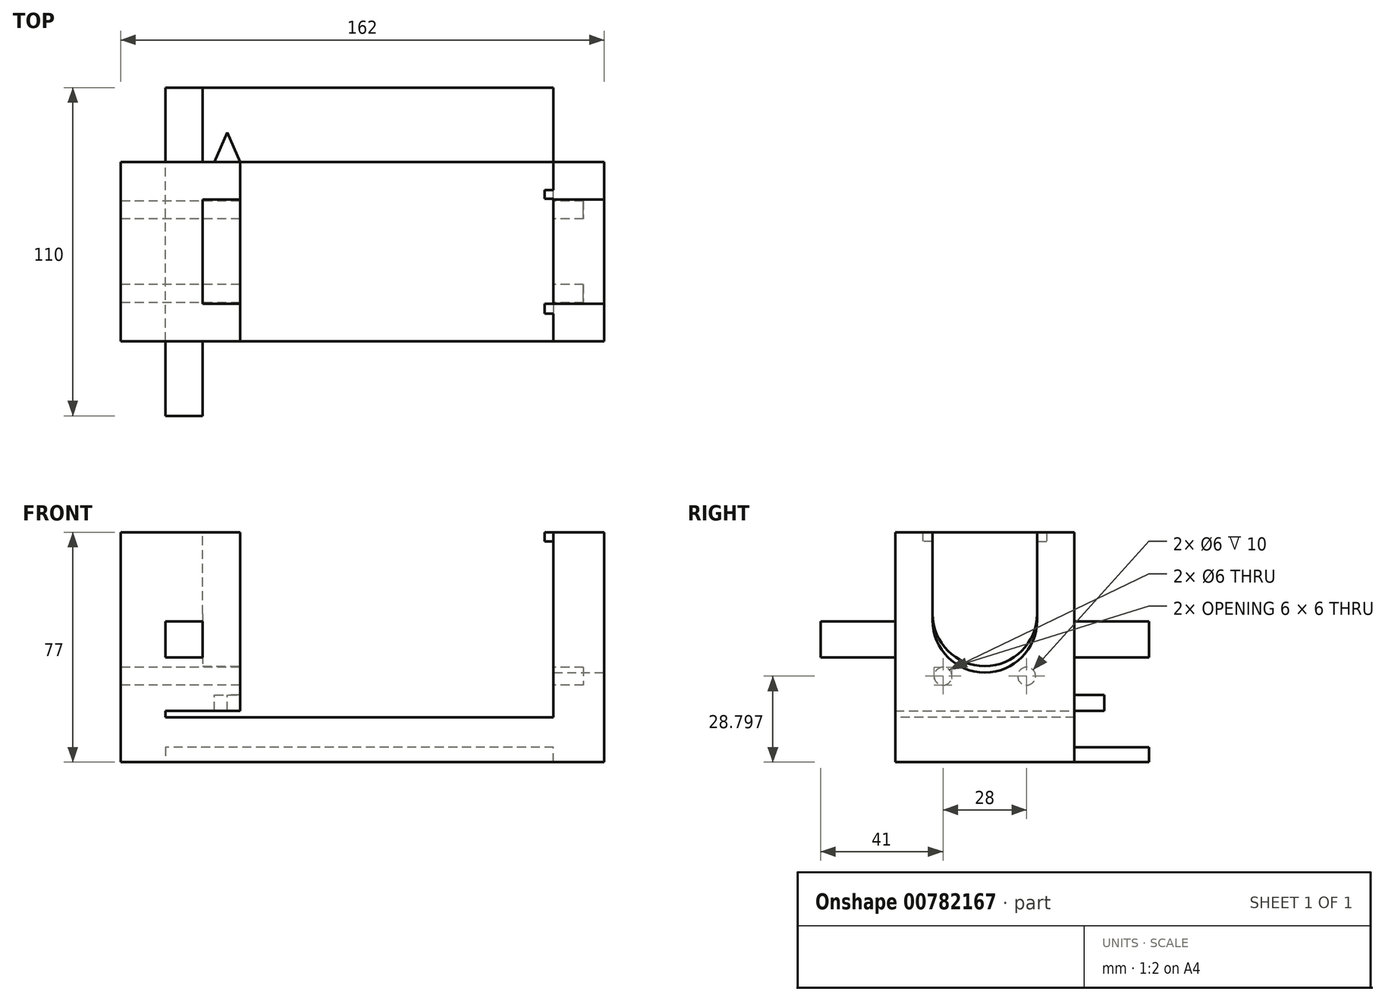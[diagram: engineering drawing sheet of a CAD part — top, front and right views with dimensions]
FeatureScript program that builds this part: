
annotation { "Feature Type Name" : "Feature", "Feature Type Description" : "" }
export const myFeature = defineFeature(function(context is Context, id is Id, definition is map)
    precondition{}
    {
        {
            var Q0;
            Q0=qCreatedBy(makeId("Top.planeOp"),FACE);
            var sketch = newSketch(context, id + "F0", { "sketchPlane" : qUnion([Q0])});
            skLineSegment(sketch, "E0.bottom", {"start": v(-65, 30) * mm, "end": v(65, 30) * mm});
            skLineSegment(sketch, "E0.top", {"start": v(-65, -30) * mm, "end": v(65, -30) * mm});
            skLineSegment(sketch, "E0.left", {"start": v(-65, 30) * mm, "end": v(-65, -30) * mm});
            skLineSegment(sketch, "E0.right", {"start": v(65, 30) * mm, "end": v(65, -30) * mm});
            skPoint(sketch, "E0.middle", {"position": v(0, 0) * mm});
            skLineSegment(sketch, "E1.bottom", {"start": v(-65, 30) * mm, "end": v(-80, 30) * mm});
            skLineSegment(sketch, "E1.top", {"start": v(-65, -30) * mm, "end": v(-80, -30) * mm});
            skLineSegment(sketch, "E1.right", {"start": v(-80, 30) * mm, "end": v(-80, -30) * mm});
            skLineSegment(sketch, "E2.bottom", {"start": v(65, 30) * mm, "end": v(82, 30) * mm});
            skLineSegment(sketch, "E2.top", {"start": v(65, -30) * mm, "end": v(82, -30) * mm});
            skLineSegment(sketch, "E2.right", {"start": v(82, 30) * mm, "end": v(82, -30) * mm});
            skSolve(sketch);
        }
        {
            var Q0;
            Q0=makeQuery(id+"F0.imprint","IMPRINT",FACE,{"disambiguationData":[TD([[makeQuery(id+"F0.imprint","IMPRINT",EDGE,{"derivedFrom":sQuery(id+"F0.wireOp",EDGE,"E1.bottom")}),1.0]])]});
            var Q1;
            Q1=makeQuery(id+"F0.imprint","IMPRINT",FACE,{"disambiguationData":[TD([[makeQuery(id+"F0.imprint","IMPRINT",EDGE,{"derivedFrom":sQuery(id+"F0.wireOp",EDGE,"E2.bottom")}),-1.0]])]});
            extrude(context, id + "F1", {"entities" : qUnion([Q0, Q1]), "depth" : 65 * mm, "offsetDistance" : 25 * mm});
        }
        {
            var Q0;
            Q0=makeQuery(id+"F0.imprint","IMPRINT",FACE,{"disambiguationData":[TD([[makeQuery(id+"F0.imprint","IMPRINT",EDGE,{"derivedFrom":sQuery(id+"F0.wireOp",EDGE,"E0.bottom")}),-1.0]])]});
            extrude(context, id + "F2", {"entities" : qUnion([Q0]), "depth" : 15 * mm, "offsetDistance" : 25 * mm});
        }
        {
            var Q0;
            Q0=makeQuery(id+"F1.opExtrude","SWEPT_FACE",FACE,{"disambiguationData":[OSD([sQuery(id+"F0.wireOp",EDGE,"E2.right")])]});
            var sketch = newSketch(context, id + "F3", { "sketchPlane" : qUnion([Q0])});
            skLineSegment(sketch, "E3", {"start": v(-30, 0) * mm, "end": v(-30, 15) * mm, "construction": true});
            skLineSegment(sketch, "E4", {"start": v(-30, 15) * mm, "end": v(30, 15) * mm, "construction": true});
            skLineSegment(sketch, "E5", {"start": v(30, 15) * mm, "end": v(30, 0) * mm, "construction": true});
            skLineSegment(sketch, "E6", {"start": v(0, 0) * mm, "end": v(0, 15) * mm, "construction": true});
            skLineSegment(sketch, "E7", {"start": v(0, 15) * mm, "end": v(0, 47.5) * mm, "construction": true});
            skCircle(sketch, "E8", {"center": v(0, 47.5) * mm, "radius": 17.5 * mm});
            skLineSegment(sketch, "E9", {"start": v(0, 47.5) * mm, "end": v(-17.5, 47.5) * mm, "construction": true});
            skLineSegment(sketch, "E10", {"start": v(-17.5, 47.5) * mm, "end": v(0, 47.5) * mm, "construction": true});
            skLineSegment(sketch, "E11", {"start": v(-17.5, 47.5) * mm, "end": v(-17.5, 65) * mm});
            skLineSegment(sketch, "E12", {"start": v(0, 47.5) * mm, "end": v(17.5, 47.5) * mm, "construction": true});
            skLineSegment(sketch, "E13", {"start": v(17.5, 47.5) * mm, "end": v(17.5, 65) * mm});
            skLineSegment(sketch, "E14", {"start": v(0, 65) * mm, "end": v(0, 15) * mm, "construction": true});
            skSolve(sketch);
        }
        {
            var Q0;
            Q0 = qSketchRegion(id + "F3", true);
            var Q1;
            {var subQ0=sQuery(id+"F3.wireOp",EDGE,"E11");Q1=makeQuery(id+"F3.imprint","IMPRINT",FACE,{"disambiguationData":[TD([[makeQuery(id+"F3.imprint","IMPRINT",EDGE,{"derivedFrom":subQ0}),-1.0]])]});}
            var Q2;
            {var subQ0=sQuery(id+"F3.wireOp",EDGE,"E13");Q2=makeQuery(id+"F3.imprint","IMPRINT",FACE,{"disambiguationData":[TD([[makeQuery(id+"F3.imprint","IMPRINT",EDGE,{"derivedFrom":subQ0}),1.0]])]});}
            extrude(context, id + "F4", {"entities" : qUnion([Q0, Q1, Q2]), "operationType" : NewBodyOperationType.REMOVE, "oppositeDirection" : true, "depth" : 17 * mm, "offsetDistance" : 25 * mm});
        }
        {
            var Q0;
            Q0=makeQuery(id+"F1.opExtrude","SWEPT_FACE",FACE,{"disambiguationData":[OSD([sQuery(id+"F0.wireOp",EDGE,"E1.right")])]});
            var sketch = newSketch(context, id + "F5", { "sketchPlane" : qUnion([Q0])});
            skLineSegment(sketch, "E15", {"start": v(-30, 0) * mm, "end": v(-30, 15.8) * mm, "construction": true});
            skLineSegment(sketch, "E16", {"start": v(-30, 15.8) * mm, "end": v(30, 15.8) * mm, "construction": true});
            skLineSegment(sketch, "E17", {"start": v(0, 15.8) * mm, "end": v(0, 65) * mm, "construction": true});
            skLineSegment(sketch, "E18", {"start": v(-14, 15.8) * mm, "end": v(-14, 28.8) * mm, "construction": true});
            skLineSegment(sketch, "E19", {"start": v(-14, 28.8) * mm, "end": v(14, 28.8) * mm, "construction": true});
            skLineSegment(sketch, "E20", {"start": v(14, 28.8) * mm, "end": v(14, 15.8) * mm, "construction": true});
            skLineSegment(sketch, "E21", {"start": v(-14, 28.8) * mm, "end": v(0, 28.8) * mm, "construction": true});
            skCircle(sketch, "E22", {"center": v(-14, 28.8) * mm, "radius": 3 * mm});
            skCircle(sketch, "E23", {"center": v(14, 28.8) * mm, "radius": 3 * mm});
            skSolve(sketch);
        }
        {
            var Q0;
            Q0 = qSketchRegion(id + "F5", true);
            extrude(context, id + "F6", {"entities" : qUnion([Q0]), "operationType" : NewBodyOperationType.REMOVE, "oppositeDirection" : true, "depth" : 155 * mm, "offsetDistance" : 25 * mm});
        }
        {
            var Q0;
            Q0=makeQuery(id+"F1.opExtrude","SWEPT_FACE",FACE,{"disambiguationData":[OSD([sQuery(id+"F0.wireOp",EDGE,"E0.left")])]});
            var sketch = newSketch(context, id + "F7", { "sketchPlane" : qUnion([Q0])});
            skLineSegment(sketch, "E24.bottom", {"start": v(-30, 65) * mm, "end": v(30, 65) * mm});
            skLineSegment(sketch, "E24.top", {"start": v(-30, 15.18) * mm, "end": v(30, 15.18) * mm});
            skLineSegment(sketch, "E24.left", {"start": v(-30, 65) * mm, "end": v(-30, 15.18) * mm});
            skLineSegment(sketch, "E24.right", {"start": v(30, 65) * mm, "end": v(30, 15.18) * mm});
            skLineSegment(sketch, "E25", {"start": v(-30, 65) * mm, "end": v(-30, 0) * mm, "construction": true});
            skSolve(sketch);
        }
        {
            var Q0;
            Q0=makeQuery(id+"F7.imprint","IMPRINT",FACE,{"disambiguationData":[TD([[makeQuery(id+"F7.imprint","IMPRINT",EDGE,{"derivedFrom":sQuery(id+"F7.wireOp",EDGE,"E24.bottom")}),1.0]])]});
            extrude(context, id + "F8", {"entities" : qUnion([Q0]), "depth" : 25 * mm, "offsetDistance" : 25 * mm});
        }
        {
            var Q0;
            Q0=makeQuery(id+"F8.opExtrude","CAP_FACE",FACE,{"disambiguationData":[OSD([sQuery(id+"F0.wireOp",EDGE,"E0.left"),sQuery(id+"F5.wireOp",EDGE,"E22"),sQuery(id+"F5.wireOp",EDGE,"E23"),sQuery(id+"F7.wireOp",EDGE,"E24.bottom"),sQuery(id+"F7.wireOp",EDGE,"E24.top"),sQuery(id+"F7.wireOp",EDGE,"E24.left"),sQuery(id+"F7.wireOp",EDGE,"E24.right")])],"isStart":false});
            var sketch = newSketch(context, id + "F9", { "sketchPlane" : qUnion([Q0])});
            skLineSegment(sketch, "E26", {"start": v(-30, 15.18) * mm, "end": v(30, 15.18) * mm, "construction": true});
            skLineSegment(sketch, "E27", {"start": v(30, 15.18) * mm, "end": v(30, 65) * mm, "construction": true});
            skLineSegment(sketch, "E28", {"start": v(30, 65) * mm, "end": v(-30, 65) * mm, "construction": true});
            skLineSegment(sketch, "E29", {"start": v(-30, 65) * mm, "end": v(-30, 15.18) * mm, "construction": true});
            skLineSegment(sketch, "E30", {"start": v(0, 15.18) * mm, "end": v(0, 65) * mm, "construction": true});
            skLineSegment(sketch, "E31", {"start": v(-30, 65) * mm, "end": v(-17.5, 65) * mm, "construction": true});
            skLineSegment(sketch, "E32", {"start": v(30, 65) * mm, "end": v(17.5, 65) * mm, "construction": true});
            skLineSegment(sketch, "E33", {"start": v(-17.5, 65) * mm, "end": v(-17.5, 15.18) * mm, "construction": true});
            skLineSegment(sketch, "E34", {"start": v(17.5, 65) * mm, "end": v(17.5, 15.18) * mm, "construction": true});
            skLineSegment(sketch, "E35", {"start": v(-17.5, 32.15) * mm, "end": v(17.5, 32.15) * mm, "construction": true});
            skLineSegment(sketch, "E36", {"start": v(0, 32.15) * mm, "end": v(0, 49.65) * mm, "construction": true});
            skCircle(sketch, "E37", {"center": v(0, 49.65) * mm, "radius": 17.5 * mm});
            skLineSegment(sketch, "E38", {"start": v(0, 49.65) * mm, "end": v(17.5, 49.65) * mm, "construction": true});
            skLineSegment(sketch, "E39", {"start": v(17.5, 49.65) * mm, "end": v(0, 49.65) * mm, "construction": true});
            skLineSegment(sketch, "E40", {"start": v(-17.5, 49.65) * mm, "end": v(0, 49.65) * mm, "construction": true});
            skLineSegment(sketch, "E41", {"start": v(17.5, 49.65) * mm, "end": v(17.5, 65) * mm});
            skLineSegment(sketch, "E42", {"start": v(-17.5, 49.65) * mm, "end": v(-17.5, 65) * mm});
            skLineSegment(sketch, "E43", {"start": v(-17.5, 65) * mm, "end": v(-8.4, 65) * mm});
            skLineSegment(sketch, "E44", {"start": v(17.5, 65) * mm, "end": v(8.4, 65) * mm});
            skSolve(sketch);
        }
        {
            var Q0;
            {var subQ0=sQuery(id+"F9.wireOp",EDGE,"E37");var subQ1=makeQuery(id+"F9.imprint","INTERSECT",VERTEX,{"derivedFrom":[subQ0,sQuery(id+"F9.wireOp",EDGE,"E41")]});Q0=makeQuery(id+"F9.imprint","IMPRINT",FACE,{"disambiguationData":[TD([[makeQuery(id+"F9.imprint","IMPRINT",EDGE,{"disambiguationData":[TD([[subQ1,1.0]])],"derivedFrom":subQ0}),1.0]])]});}
            var Q1;
            {var subQ0=sQuery(id+"F9.wireOp",EDGE,"E41");Q1=makeQuery(id+"F9.imprint","IMPRINT",FACE,{"disambiguationData":[TD([[makeQuery(id+"F9.imprint","IMPRINT",EDGE,{"derivedFrom":subQ0}),1.0]])]});}
            var Q2;
            {var subQ0=sQuery(id+"F9.wireOp",EDGE,"E42");Q2=makeQuery(id+"F9.imprint","IMPRINT",FACE,{"disambiguationData":[TD([[makeQuery(id+"F9.imprint","IMPRINT",EDGE,{"derivedFrom":subQ0}),-1.0]])]});}
            extrude(context, id + "F10", {"entities" : qUnion([Q0, Q1, Q2]), "operationType" : NewBodyOperationType.REMOVE, "oppositeDirection" : true, "depth" : 12.5 * mm, "offsetDistance" : 25 * mm});
        }
        {
            var Q0;
            Q0=makeQuery(id+"F1.opExtrude","SWEPT_BODY",BODY,{"disambiguationData":[OSD([sQuery(id+"F0.wireOp",EDGE,"E2.bottom"),sQuery(id+"F0.wireOp",EDGE,"E2.top"),sQuery(id+"F0.wireOp",EDGE,"E0.right"),sQuery(id+"F0.wireOp",EDGE,"E2.right")])]});
            var Q1;
            Q1=makeQuery(id+"F2.opExtrude","SWEPT_BODY",BODY,{"disambiguationData":[OSD([sQuery(id+"F0.wireOp",EDGE,"E0.bottom"),sQuery(id+"F0.wireOp",EDGE,"E0.top"),sQuery(id+"F0.wireOp",EDGE,"E0.left"),sQuery(id+"F0.wireOp",EDGE,"E0.right")])]});
            var Q2;
            Q2=makeQuery(id+"F1.opExtrude","SWEPT_BODY",BODY,{"disambiguationData":[OSD([sQuery(id+"F0.wireOp",EDGE,"E1.bottom"),sQuery(id+"F0.wireOp",EDGE,"E1.top"),sQuery(id+"F0.wireOp",EDGE,"E0.left"),sQuery(id+"F0.wireOp",EDGE,"E1.right")])]});
            booleanBodies(context, id + "F11", {"operationType" : BooleanOperationType.UNION, "tools" : qUnion([Q0, Q1, Q2])});
        }
        {
            var Q0;
            Q0=makeQuery(id+"F8.opExtrude","SWEPT_FACE",FACE,{"disambiguationData":[OSD([sQuery(id+"F7.wireOp",EDGE,"E24.top")])]});
            var sketch = newSketch(context, id + "F12", { "sketchPlane" : qUnion([Q0])});
            skSolve(sketch);
        }
        {
            var Q0;
            Q0 = qSketchRegion(id + "F12", true);
            var Q1;
            {var subQ0=sQuery(id+"F7.wireOp",EDGE,"E24.top");Q1=makeQuery(id+"F12.imprint","IMPRINT",FACE,{"disambiguationData":[TD([[makeQuery(id+"F12.imprint","IMPRINT",EDGE,{"derivedFrom":makeQuery(id+"F8.opExtrude","CAP_EDGE",EDGE,{"disambiguationData":[OSD([subQ0])],"isStart":true})}),1.0]])]});}
            extrude(context, id + "F13", {"entities" : qUnion([Q0, Q1]), "operationType" : NewBodyOperationType.REMOVE, "oppositeDirection" : true, "depth" : 2 * mm, "offsetDistance" : 25 * mm});
        }
        {
            var Q0;
            Q0=makeQuery(id+"F11.opBoolean","MERGE",FACE,{"derivedFrom":[makeQuery(id+"F1.opExtrude","SWEPT_FACE",FACE,{"disambiguationData":[OSD([sQuery(id+"F0.wireOp",EDGE,"E1.bottom")])]}),makeQuery(id+"F1.opExtrude","SWEPT_FACE",FACE,{"disambiguationData":[OSD([sQuery(id+"F0.wireOp",EDGE,"E2.bottom")])]}),makeQuery(id+"F2.opExtrude","SWEPT_FACE",FACE,{"disambiguationData":[OSD([sQuery(id+"F0.wireOp",EDGE,"E0.bottom")])]})]});
            var sketch = newSketch(context, id + "F14", { "sketchPlane" : qUnion([Q0])});
            skLineSegment(sketch, "E45", {"start": v(-65, 0) * mm, "end": v(65, 0) * mm});
            skLineSegment(sketch, "E46", {"start": v(-65, 0) * mm, "end": v(-65, 5) * mm});
            skLineSegment(sketch, "E47", {"start": v(-65, 5) * mm, "end": v(64.92, 5) * mm});
            skLineSegment(sketch, "E48", {"start": v(64.92, 5) * mm, "end": v(65, 0) * mm});
            skSolve(sketch);
        }
        {
            var Q0;
            Q0 = qSketchRegion(id + "F14", true);
            extrude(context, id + "F15", {"entities" : qUnion([Q0]), "operationType" : NewBodyOperationType.ADD, "depth" : 25 * mm, "offsetDistance" : 25 * mm});
        }
        {
            var Q0;
            Q0=makeQuery(id+"F8.opExtrude","SWEPT_FACE",FACE,{"disambiguationData":[OSD([sQuery(id+"F7.wireOp",EDGE,"E24.left")])]});
            var sketch = newSketch(context, id + "F16", { "sketchPlane" : qUnion([Q0])});
            skLineSegment(sketch, "E49", {"start": v(-65, 65) * mm, "end": v(-65, 17.18) * mm, "construction": true});
            skLineSegment(sketch, "E50", {"start": v(-65, 17.18) * mm, "end": v(-40, 17.18) * mm, "construction": true});
            skLineSegment(sketch, "E51", {"start": v(-65, 17.18) * mm, "end": v(-65, 41.1) * mm, "construction": true});
            skLineSegment(sketch, "E52", {"start": v(-65, 41.1) * mm, "end": v(-40, 41.1) * mm, "construction": true});
            skLineSegment(sketch, "E53", {"start": v(-65, 41.1) * mm, "end": v(-65, 47.1) * mm, "construction": true});
            skLineSegment(sketch, "E54", {"start": v(-65, 47.1) * mm, "end": v(-65, 41.1) * mm, "construction": true});
            skLineSegment(sketch, "E55", {"start": v(-65, 41.1) * mm, "end": v(-65, 35.1) * mm, "construction": true});
            skLineSegment(sketch, "E56", {"start": v(-65, 35.1) * mm, "end": v(-65, 41.1) * mm, "construction": true});
            skLineSegment(sketch, "E57", {"start": v(-65, 47.1) * mm, "end": v(-65, 35.1) * mm});
            skLineSegment(sketch, "E58", {"start": v(-52.5, 35.1) * mm, "end": v(-52.5, 47.1) * mm});
            skPoint(sketch, "E58.startSnap0", {"position": v(-52.5, 17.18) * mm});
            skLineSegment(sketch, "E59", {"start": v(-52.5, 47.1) * mm, "end": v(-65, 47.1) * mm});
            skLineSegment(sketch, "E60", {"start": v(-65, 35.1) * mm, "end": v(-52.5, 35.1) * mm});
            skSolve(sketch);
        }
        {
            var Q0;
            Q0 = qSketchRegion(id + "F16", true);
            extrude(context, id + "F17", {"entities" : qUnion([Q0]), "depth" : 25 * mm, "offsetDistance" : 25 * mm});
        }
        {
            var Q0;
            Q0 = qSketchRegion(id + "F16", true);
            extrude(context, id + "F18", {"entities" : qUnion([Q0]), "depth" : 25 * mm, "offsetDistance" : 25 * mm});
        }
        {
            var Q0;
            Q0=makeQuery(id+"F8.opExtrude","SWEPT_FACE",FACE,{"disambiguationData":[OSD([sQuery(id+"F7.wireOp",EDGE,"E24.right")])]});
            var sketch = newSketch(context, id + "F19", { "sketchPlane" : qUnion([Q0])});
            skLineSegment(sketch, "E61", {"start": v(40, 65) * mm, "end": v(40, 17.18) * mm, "construction": true});
            skLineSegment(sketch, "E62", {"start": v(40, 17.18) * mm, "end": v(65, 17.18) * mm, "construction": true});
            skLineSegment(sketch, "E63", {"start": v(65, 17.18) * mm, "end": v(65, 65) * mm, "construction": true});
            skLineSegment(sketch, "E64", {"start": v(65, 65) * mm, "end": v(40, 65) * mm, "construction": true});
            skLineSegment(sketch, "E65", {"start": v(65, 41.1) * mm, "end": v(40, 41.1) * mm, "construction": true});
            skLineSegment(sketch, "E66", {"start": v(40, 41.1) * mm, "end": v(52.5, 41.1) * mm, "construction": true});
            skLineSegment(sketch, "E67", {"start": v(52.5, 41.1) * mm, "end": v(52.5, 65) * mm, "construction": true});
            skLineSegment(sketch, "E68", {"start": v(52.5, 65) * mm, "end": v(52.5, 17.18) * mm, "construction": true});
            skLineSegment(sketch, "E69", {"start": v(65, 41.1) * mm, "end": v(65, 47.1) * mm, "construction": true});
            skLineSegment(sketch, "E70", {"start": v(65, 47.1) * mm, "end": v(65, 41.1) * mm, "construction": true});
            skLineSegment(sketch, "E71", {"start": v(65, 41.1) * mm, "end": v(65, 35.1) * mm, "construction": true});
            skLineSegment(sketch, "E72", {"start": v(65, 47.1) * mm, "end": v(65, 35.1) * mm});
            skLineSegment(sketch, "E73", {"start": v(65, 47.1) * mm, "end": v(52.5, 47.1) * mm});
            skLineSegment(sketch, "E74", {"start": v(52.5, 47.1) * mm, "end": v(52.5, 35.1) * mm});
            skLineSegment(sketch, "E75", {"start": v(52.5, 35.1) * mm, "end": v(65, 35.1) * mm});
            skSolve(sketch);
        }
        {
            var Q0;
            Q0 = qSketchRegion(id + "F19", true);
            extrude(context, id + "F20", {"entities" : qUnion([Q0]), "operationType" : NewBodyOperationType.ADD, "depth" : 25 * mm, "offsetDistance" : 25 * mm});
        }
        {
            var Q0;
            Q0=makeQuery(id+"F8.opExtrude","SWEPT_FACE",FACE,{"disambiguationData":[OSD([sQuery(id+"F7.wireOp",EDGE,"E24.bottom")])]});
            extrude(context, id + "F21", {"entities" : qUnion([Q0]), "operationType" : NewBodyOperationType.ADD, "depth" : 12 * mm, "offsetDistance" : 25 * mm});
        }
        {
            var Q0;
            {var subQ0=sQuery(id+"F7.wireOp",EDGE,"E24.right");Q0=makeQuery(id+"F21.boolean.opBoolean","MERGE",FACE,{"derivedFrom":[makeQuery(id+"F8.opExtrude","SWEPT_FACE",FACE,{"disambiguationData":[OSD([subQ0])]}),makeQuery(id+"F21.opExtrude","SWEPT_FACE",FACE,{"disambiguationData":[OSD([sQuery(id+"F7.wireOp",EDGE,"E24.bottom"),subQ0])]})]});}
            var sketch = newSketch(context, id + "F22", { "sketchPlane" : qUnion([Q0])});
            skLineSegment(sketch, "E76", {"start": v(40, 17.18) * mm, "end": v(48.6, 17.18) * mm});
            skLineSegment(sketch, "E77", {"start": v(48.6, 17.18) * mm, "end": v(48.6, 22.47) * mm});
            skLineSegment(sketch, "E78", {"start": v(48.6, 22.47) * mm, "end": v(40, 22.47) * mm});
            skLineSegment(sketch, "E79", {"start": v(40, 22.47) * mm, "end": v(40, 17.18) * mm});
            skSolve(sketch);
        }
        {
            var Q0;
            Q0 = qSketchRegion(id + "F22", true);
            extrude(context, id + "F23", {"entities" : qUnion([Q0]), "operationType" : NewBodyOperationType.ADD, "depth" : 10 * mm, "offsetDistance" : 25 * mm});
        }
        {
            var Q0;
            Q0=makeQuery(id+"F23.opExtrude","SWEPT_FACE",FACE,{"disambiguationData":[OSD([sQuery(id+"F22.wireOp",EDGE,"E78")])]});
            var sketch = newSketch(context, id + "F24", { "sketchPlane" : qUnion([Q0])});
            skLineSegment(sketch, "E80", {"start": v(-40, 40) * mm, "end": v(-48.6, 30) * mm, "construction": true});
            skLineSegment(sketch, "E81", {"start": v(-48.6, 30) * mm, "end": v(-40, 30) * mm, "construction": true});
            skLineSegment(sketch, "E82", {"start": v(-40, 30) * mm, "end": v(-48.6, 40) * mm, "construction": true});
            skLineSegment(sketch, "E83", {"start": v(-40, 40) * mm, "end": v(-44.3, 40) * mm, "construction": true});
            skLineSegment(sketch, "E84", {"start": v(-44.3, 40) * mm, "end": v(-48.6, 40) * mm, "construction": true});
            skLineSegment(sketch, "E85", {"start": v(-40, 30) * mm, "end": v(-44.3, 40) * mm});
            skLineSegment(sketch, "E86", {"start": v(-48.6, 30) * mm, "end": v(-44.3, 40) * mm});
            skLineSegment(sketch, "E87", {"start": v(-48.6, 30) * mm, "end": v(-40, 30) * mm});
            skLineSegment(sketch, "E88", {"start": v(-44.3, 40) * mm, "end": v(-40, 40) * mm});
            skLineSegment(sketch, "E89", {"start": v(-40, 30) * mm, "end": v(-48.6, 30) * mm});
            skLineSegment(sketch, "E90", {"start": v(-48.6, 40) * mm, "end": v(-44.3, 40) * mm});
            skLineSegment(sketch, "E91", {"start": v(-48.6, 40) * mm, "end": v(-48.6, 30) * mm});
            skSolve(sketch);
        }
        {
            var Q0;
            Q0=makeQuery(id+"F24.imprint","IMPRINT",FACE,{"disambiguationData":[TD([[makeQuery(id+"F24.imprint","IMPRINT",EDGE,{"derivedFrom":sQuery(id+"F24.wireOp",EDGE,"E85")}),-1.0]])]});
            var Q1;
            Q1=makeQuery(id+"F24.imprint","IMPRINT",FACE,{"disambiguationData":[TD([[makeQuery(id+"F24.imprint","IMPRINT",EDGE,{"derivedFrom":sQuery(id+"F24.wireOp",EDGE,"E86")}),1.0]])]});
            extrude(context, id + "F25", {"entities" : qUnion([Q0, Q1]), "operationType" : NewBodyOperationType.REMOVE, "oppositeDirection" : true, "depth" : 10 * mm, "offsetDistance" : 25 * mm});
        }
        {
            var Q0;
            {var subQ0=sQuery(id+"F0.wireOp",EDGE,"E2.top");var subQ1=sQuery(id+"F0.wireOp",EDGE,"E0.right");var subQ2=sQuery(id+"F0.wireOp",EDGE,"E2.right");Q0=makeQuery(id+"F4.boolean.opBoolean","SPLIT",FACE,{"disambiguationData":[TD([makeQuery(id+"F1.opExtrude","SWEPT_FACE",FACE,{"disambiguationData":[OSD([subQ0])]})])],"derivedFrom":makeQuery(id+"F1.opExtrude","CAP_FACE",FACE,{"disambiguationData":[OSD([sQuery(id+"F0.wireOp",EDGE,"E2.bottom"),subQ0,subQ1,subQ2])],"isStart":false})});}
            var Q1;
            {var subQ0=sQuery(id+"F0.wireOp",EDGE,"E2.bottom");var subQ1=sQuery(id+"F0.wireOp",EDGE,"E2.right");var subQ2=sQuery(id+"F0.wireOp",EDGE,"E0.right");Q1=makeQuery(id+"F4.boolean.opBoolean","SPLIT",FACE,{"disambiguationData":[TD([makeQuery(id+"F1.opExtrude","SWEPT_FACE",FACE,{"disambiguationData":[OSD([subQ0])]})])],"derivedFrom":makeQuery(id+"F1.opExtrude","CAP_FACE",FACE,{"disambiguationData":[OSD([subQ0,sQuery(id+"F0.wireOp",EDGE,"E2.top"),subQ2,subQ1])],"isStart":false})});}
            extrude(context, id + "F26", {"entities" : qUnion([Q0, Q1]), "operationType" : NewBodyOperationType.ADD, "depth" : 12 * mm, "offsetDistance" : 25 * mm});
        }
        {
            var Q0;
            {var subQ0=sQuery(id+"F0.wireOp",EDGE,"E0.right");var subQ1=sQuery(id+"F0.wireOp",EDGE,"E2.top");var subQ3=makeQuery(id+"F1.opExtrude","SWEPT_FACE",FACE,{"disambiguationData":[OSD([subQ1])]});var subQ4=makeQuery(id+"F1.opExtrude","SWEPT_FACE",FACE,{"disambiguationData":[OSD([subQ0])]});Q0=makeQuery(id+"F26.boolean.opBoolean","MERGE",FACE,{"derivedFrom":[makeQuery(id+"F11.opBoolean","SPLIT",FACE,{"disambiguationData":[TD([makeQuery(id+"F1.opExtrude","SWEPT_FACE",FACE,{"disambiguationData":[OSD([sQuery(id+"F0.wireOp",EDGE,"E1.top")])]})])],"derivedFrom":subQ4}),makeQuery(id+"F26.opExtrude","SWEPT_FACE",FACE,{"disambiguationData":[OSD([subQ0]),TDD([makeQuery(id+"F4.boolean.opBoolean","SPLIT",EDGE,{"disambiguationData":[TD([subQ3])],"derivedFrom":makeQuery(id+"F1.opExtrude","CAP_EDGE",EDGE,{"disambiguationData":[OSD([subQ0])],"isStart":false})})])]})]});}
            var sketch = newSketch(context, id + "F27", { "sketchPlane" : qUnion([Q0])});
            skLineSegment(sketch, "E92.bottom", {"start": v(17.5, 77) * mm, "end": v(20.78, 77) * mm});
            skLineSegment(sketch, "E92.top", {"start": v(17.5, 73.91) * mm, "end": v(20.78, 73.91) * mm});
            skLineSegment(sketch, "E92.left", {"start": v(17.5, 77) * mm, "end": v(17.5, 73.91) * mm});
            skLineSegment(sketch, "E92.right", {"start": v(20.78, 77) * mm, "end": v(20.78, 73.91) * mm});
            skLineSegment(sketch, "E93.bottom", {"start": v(-17.7, 77) * mm, "end": v(-20.72, 77) * mm});
            skLineSegment(sketch, "E93.top", {"start": v(-17.7, 73.91) * mm, "end": v(-20.72, 73.91) * mm});
            skLineSegment(sketch, "E93.left", {"start": v(-17.7, 77) * mm, "end": v(-17.7, 73.91) * mm});
            skLineSegment(sketch, "E93.right", {"start": v(-20.72, 77) * mm, "end": v(-20.72, 73.91) * mm});
            skSolve(sketch);
        }
        {
            var Q0;
            Q0=makeQuery(id+"F27.imprint","IMPRINT",FACE,{"disambiguationData":[TD([[makeQuery(id+"F27.imprint","IMPRINT",EDGE,{"derivedFrom":sQuery(id+"F27.wireOp",EDGE,"xnt3S6Cn-In4g-HvGt-EqnQ-VhXPL2CSZe8M.bottom")}),-1.0]])]});
            var Q1;
            Q1=makeQuery(id+"F27.imprint","IMPRINT",FACE,{"disambiguationData":[TD([[makeQuery(id+"F27.imprint","IMPRINT",EDGE,{"derivedFrom":sQuery(id+"F27.wireOp",EDGE,"0XkRLyHb-z8qZ-4mP7-7JuY-5aOf4k6SaSlp.bottom")}),-1.0]])]});
            var Q2;
            Q2=makeQuery(id+"F27.imprint","IMPRINT",FACE,{"disambiguationData":[TD([[makeQuery(id+"F27.imprint","IMPRINT",EDGE,{"derivedFrom":sQuery(id+"F27.wireOp",EDGE,"E92.bottom")}),-1.0]])]});
            var Q3;
            Q3=makeQuery(id+"F27.imprint","IMPRINT",FACE,{"disambiguationData":[TD([[makeQuery(id+"F27.imprint","IMPRINT",EDGE,{"derivedFrom":sQuery(id+"F27.wireOp",EDGE,"E93.bottom")}),1.0]])]});
            var Q4;
            Q4=makeQuery(id+"F27.imprint","IMPRINT",FACE,{"disambiguationData":[TD([[makeQuery(id+"F27.imprint","IMPRINT",EDGE,{"derivedFrom":sQuery(id+"F27.wireOp",EDGE,"E93.bottom")}),-1.0]])]});
            extrude(context, id + "F28", {"entities" : qUnion([Q0, Q1, Q2, Q3, Q4]), "operationType" : NewBodyOperationType.ADD, "depth" : 3 * mm, "offsetDistance" : 25 * mm});
        }
        {
            var Q0;
            Q0=makeQuery(id+"F18.opExtrude","SWEPT_BODY",BODY,{"disambiguationData":[OSD([sQuery(id+"F16.wireOp",EDGE,"E57"),sQuery(id+"F16.wireOp",EDGE,"E58"),sQuery(id+"F16.wireOp",EDGE,"E59"),sQuery(id+"F16.wireOp",EDGE,"E60")])]});
            deleteBodies(context, id + "F29", {"entities" : qUnion([Q0])});
        }
    });
